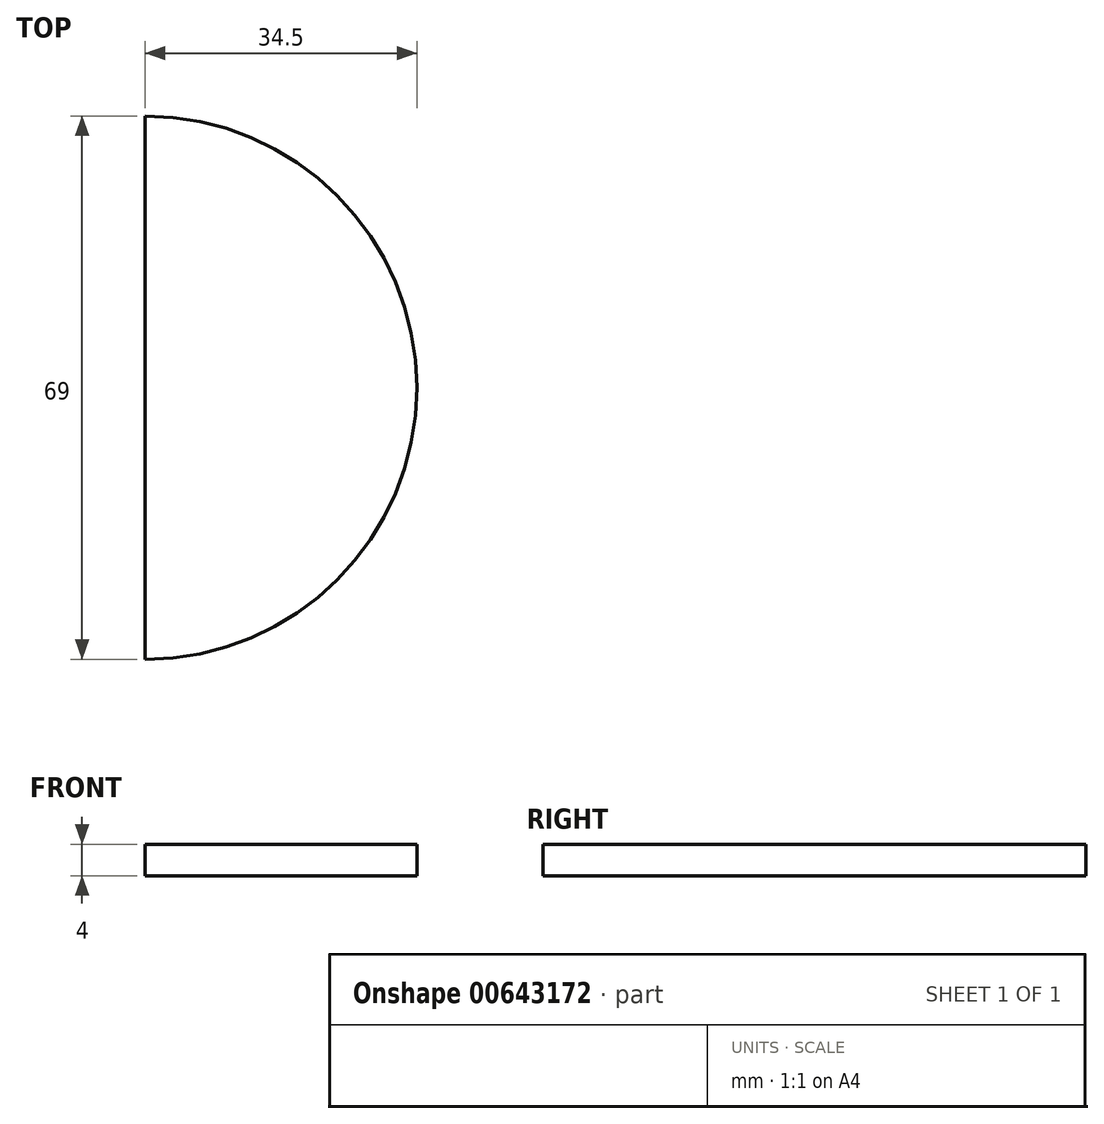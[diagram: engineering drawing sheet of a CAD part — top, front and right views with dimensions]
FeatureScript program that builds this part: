
annotation { "Feature Type Name" : "Feature", "Feature Type Description" : "" }
export const myFeature = defineFeature(function(context is Context, id is Id, definition is map)
    precondition{}
    {
        {
            var Q0;
            Q0=qCreatedBy(makeId("Top.planeOp"),FACE);
            var sketch = newSketch(context, id + "F0", { "sketchPlane" : qUnion([Q0])});
            skArc(sketch, "E0", {"start": v(0, -34.5) * mm, "mid": v(34.5, 0) * mm, "end": v(0, 34.5) * mm});
            skLineSegment(sketch, "E1", {"start": v(0, 40.92) * mm, "end": v(0, -47.64) * mm});
            skArc(sketch, "E2.MirrorCS", {"start": v(0, -34.5) * mm, "mid": v(-34.5, 0) * mm, "end": v(0, 34.5) * mm});
            skSolve(sketch);
        }
        {
            var Q0;
            {var subQ0=sQuery(id+"F0.wireOp",EDGE,"E0");Q0=makeQuery(id+"F0.imprint","IMPRINT",FACE,{"disambiguationData":[TD([[makeQuery(id+"F0.imprint","IMPRINT",EDGE,{"derivedFrom":subQ0}),1.0]])]});}
            extrude(context, id + "F1", {"entities" : qUnion([Q0]), "depth" : 4 * mm, "offsetDistance" : 25 * mm});
        }
    });
